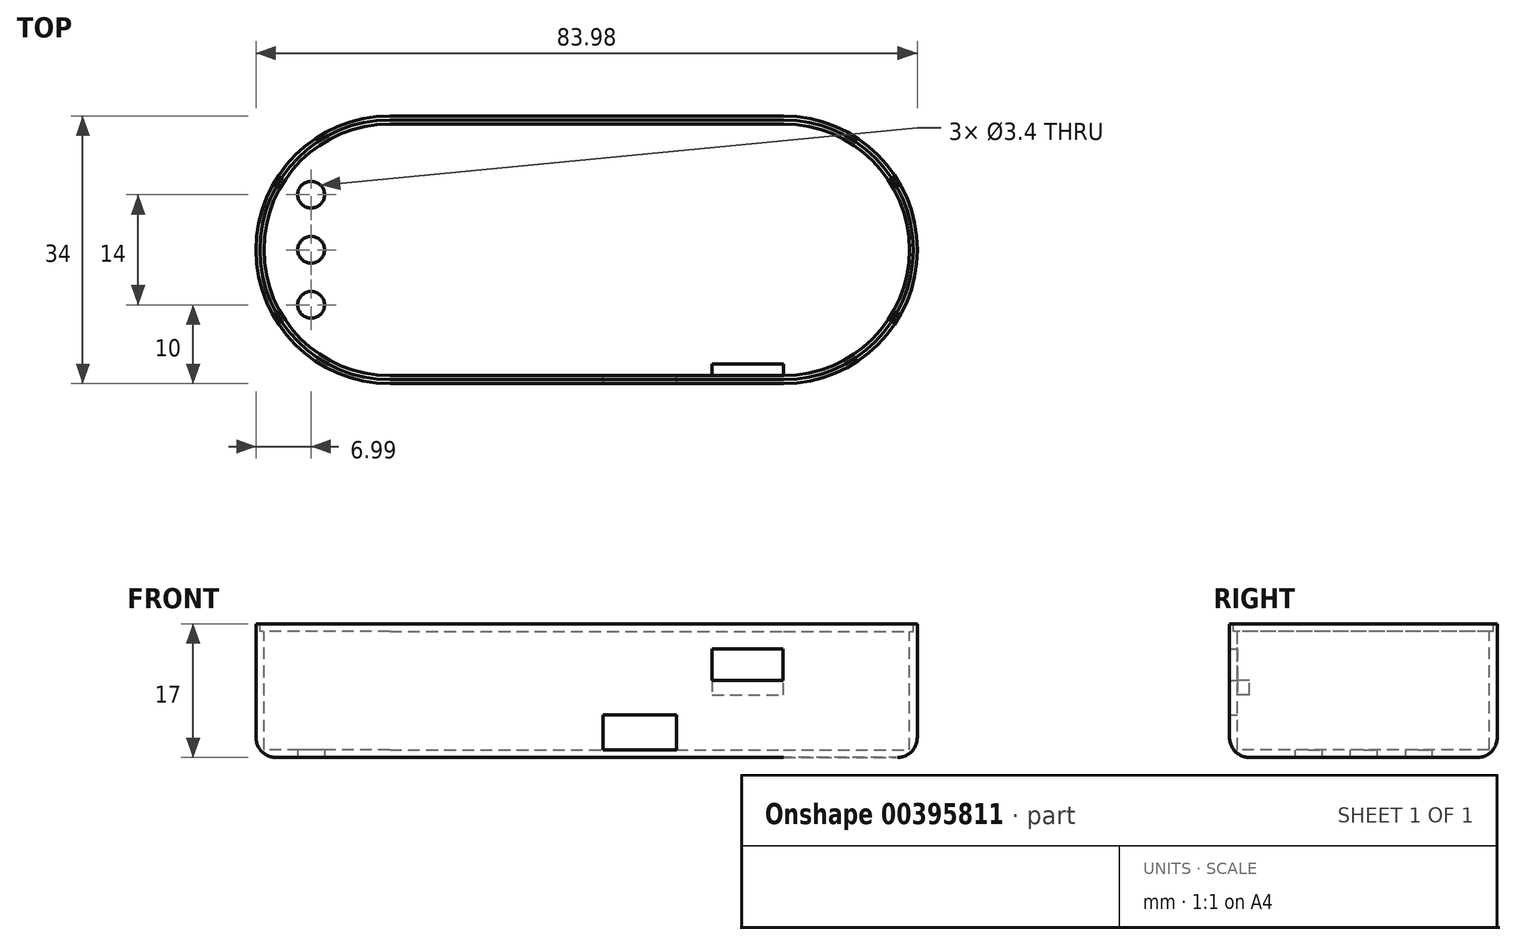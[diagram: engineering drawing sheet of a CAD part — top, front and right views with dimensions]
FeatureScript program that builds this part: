
annotation { "Feature Type Name" : "Feature", "Feature Type Description" : "" }
export const myFeature = defineFeature(function(context is Context, id is Id, definition is map)
    precondition{}
    {
        {
            var Q0;
            Q0=qCreatedBy(makeId("Top.planeOp"),FACE);
            var sketch = newSketch(context, id + "F0", { "sketchPlane" : qUnion([Q0])});
            skLineSegment(sketch, "E0.bottom", {"start": v(-25, 17) * mm, "end": v(25, 17) * mm});
            skLineSegment(sketch, "E0.top", {"start": v(-25, -17) * mm, "end": v(25, -17) * mm});
            skPoint(sketch, "E0.middle", {"position": v(0, 0) * mm});
            skPoint(sketch, "E1", {"position": v(25, 0) * mm});
            skPoint(sketch, "E2", {"position": v(-25, 0) * mm});
            skArc(sketch, "E3", {"start": v(-25, 17) * mm, "mid": v(-42, 0) * mm, "end": v(-25, -17) * mm});
            skArc(sketch, "E4", {"start": v(25, 17) * mm, "mid": v(42, 0) * mm, "end": v(25, -17) * mm});
            skPoint(sketch, "E5", {"position": v(-42, 0) * mm});
            skPoint(sketch, "E6", {"position": v(42, 0) * mm});
            skSolve(sketch);
        }
        {
            var Q0;
            Q0 = qSketchRegion(id + "F0", true);
            extrude(context, id + "F1", {"entities" : qUnion([Q0]), "offsetDistance" : 25.4 * mm, "depth" : 17 * mm});
        }
        {
            var Q0;
            Q0=makeQuery(id+"F1.opExtrude","CAP_FACE",FACE,{"disambiguationData":[OSD([sQuery(id+"F0.wireOp",EDGE,"E0.bottom"),sQuery(id+"F0.wireOp",EDGE,"E0.top"),sQuery(id+"F0.wireOp",EDGE,"E3"),sQuery(id+"F0.wireOp",EDGE,"E4")])],"isStart":false});
            var sketch = newSketch(context, id + "F2", { "sketchPlane" : qUnion([Q0])});
            skPoint(sketch, "E7", {"position": v(-25, 16.5) * mm});
            skPoint(sketch, "E8", {"position": v(25, 16.5) * mm});
            skPoint(sketch, "E9", {"position": v(-25, -16.5) * mm});
            skPoint(sketch, "E10", {"position": v(25, -16.5) * mm});
            skLineSegment(sketch, "E11.bottom", {"start": v(-25, 16.5) * mm, "end": v(25, 16.5) * mm});
            skLineSegment(sketch, "E11.top", {"start": v(-25, -16.5) * mm, "end": v(25, -16.5) * mm});
            skArc(sketch, "E12", {"start": v(-25, 16.5) * mm, "mid": v(-41.5, 0) * mm, "end": v(-25, -16.5) * mm});
            skArc(sketch, "E13", {"start": v(25, 16.5) * mm, "mid": v(41.5, 0) * mm, "end": v(25, -16.5) * mm});
            skSolve(sketch);
        }
        {
            var Q0;
            Q0 = qSketchRegion(id + "F2", true);
            extrude(context, id + "F3", {"entities" : qUnion([Q0]), "operationType" : NewBodyOperationType.REMOVE, "oppositeDirection" : true, "depth" : 1 * mm});
        }
        {
            var Q0;
            Q0=makeQuery(id+"F3.boolean.opBoolean","COPY",FACE,{"derivedFrom":makeQuery(id+"F3.opExtrude","CAP_FACE",FACE,{"disambiguationData":[OSD([sQuery(id+"F2.wireOp",EDGE,"E11.bottom"),sQuery(id+"F2.wireOp",EDGE,"E11.top"),sQuery(id+"F2.wireOp",EDGE,"E12"),sQuery(id+"F2.wireOp",EDGE,"E13")])],"isStart":false})});
            var sketch = newSketch(context, id + "F4", { "sketchPlane" : qUnion([Q0])});
            skPoint(sketch, "E14", {"position": v(-25, 16) * mm});
            skPoint(sketch, "E15", {"position": v(-25, -16) * mm});
            skPoint(sketch, "E16", {"position": v(25, 16) * mm});
            skPoint(sketch, "E17", {"position": v(25, -16) * mm});
            skArc(sketch, "E18", {"start": v(-25, 16) * mm, "mid": v(-41, 0) * mm, "end": v(-25, -16) * mm});
            skArc(sketch, "E19", {"start": v(25, 16) * mm, "mid": v(41, 0) * mm, "end": v(25, -16) * mm});
            skLineSegment(sketch, "E20", {"start": v(-25, 16) * mm, "end": v(25, 16) * mm});
            skLineSegment(sketch, "E21", {"start": v(-25, -16) * mm, "end": v(25, -16) * mm});
            skSolve(sketch);
        }
        {
            var Q0;
            Q0 = qSketchRegion(id + "F4", true);
            extrude(context, id + "F5", {"entities" : qUnion([Q0]), "operationType" : NewBodyOperationType.REMOVE, "oppositeDirection" : true, "depth" : 15 * mm});
        }
        {
            var Q0;
            Q0=makeQuery(id+"F1.opExtrude","CAP_FACE",FACE,{"disambiguationData":[OSD([sQuery(id+"F0.wireOp",EDGE,"E0.bottom"),sQuery(id+"F0.wireOp",EDGE,"E0.top"),sQuery(id+"F0.wireOp",EDGE,"E3"),sQuery(id+"F0.wireOp",EDGE,"E4")])],"isStart":true});
            var sketch = newSketch(context, id + "F6", { "sketchPlane" : qUnion([Q0])});
            skPoint(sketch, "E22", {"position": v(-35, 7) * mm});
            skPoint(sketch, "E23", {"position": v(-35, 0) * mm});
            skPoint(sketch, "E24", {"position": v(-35, -7) * mm});
            skCircle(sketch, "E25", {"center": v(-35, -7) * mm, "radius": 1.7 * mm});
            skPoint(sketch, "E26", {"position": v(0, 7) * mm});
            skPoint(sketch, "E27", {"position": v(0, -7) * mm});
            skCircle(sketch, "E28", {"center": v(-35, 0) * mm, "radius": 1.7 * mm});
            skCircle(sketch, "E29", {"center": v(-35, 7) * mm, "radius": 1.7 * mm});
            skLineSegment(sketch, "E30", {"start": v(-35, -7) * mm, "end": v(0, -7) * mm});
            skLineSegment(sketch, "E31", {"start": v(0, 0) * mm, "end": v(-35, 0) * mm});
            skLineSegment(sketch, "E32", {"start": v(-30.27, -15.26) * mm, "end": v(-30.27, 14.86) * mm});
            skSolve(sketch);
        }
        {
            var Q0;
            Q0=makeQuery(id+"F5.boolean.opBoolean","COPY",FACE,{"derivedFrom":makeQuery(id+"F5.opExtrude","SWEPT_FACE",FACE,{"disambiguationData":[OSD([sQuery(id+"F4.wireOp",EDGE,"E21")])]})});
            var sketch = newSketch(context, id + "F7", { "sketchPlane" : qUnion([Q0])});
            skPoint(sketch, "E33", {"position": v(-11.39, 1) * mm});
            skLineSegment(sketch, "E34.left", {"start": v(-11.39, 1) * mm, "end": v(-11.39, 5.4) * mm});
            skLineSegment(sketch, "E35.bottom", {"start": v(-15.94, 13.82) * mm, "end": v(-24.94, 13.82) * mm});
            skLineSegment(sketch, "E35.top", {"start": v(-15.94, 9.82) * mm, "end": v(-24.94, 9.82) * mm});
            skLineSegment(sketch, "E35.left", {"start": v(-15.94, 13.82) * mm, "end": v(-15.94, 9.82) * mm});
            skLineSegment(sketch, "E35.right", {"start": v(-24.94, 13.82) * mm, "end": v(-24.94, 9.82) * mm});
            skPoint(sketch, "E36.orphan", {"position": v(-20.99, 10.26) * mm});
            skPoint(sketch, "E37.orphan", {"position": v(-20.99, 16.75) * mm});
            skPoint(sketch, "E38", {"position": v(-2.09, 1) * mm});
            skLineSegment(sketch, "E39.bottom", {"start": v(-2.09, 1) * mm, "end": v(-11.39, 1) * mm});
            skLineSegment(sketch, "E39.top", {"start": v(-2.09, 5.4) * mm, "end": v(-11.39, 5.4) * mm});
            skLineSegment(sketch, "E39.left", {"start": v(-2.09, 1) * mm, "end": v(-2.09, 5.4) * mm});
            skLineSegment(sketch, "E40.bottom", {"start": v(-15.94, 9.82) * mm, "end": v(-25, 9.82) * mm});
            skLineSegment(sketch, "E40.top", {"start": v(-15.94, 7.17) * mm, "end": v(-25, 7.17) * mm});
            skLineSegment(sketch, "E40.left", {"start": v(-15.94, 9.82) * mm, "end": v(-15.94, 7.17) * mm});
            skLineSegment(sketch, "E40.right", {"start": v(-25, 9.82) * mm, "end": v(-25, 7.17) * mm});
            skSolve(sketch);
        }
        {
            var Q0;
            Q0=makeQuery(id+"F7.imprint","IMPRINT",FACE,{"disambiguationData":[TD([[makeQuery(id+"F7.imprint","IMPRINT",EDGE,{"derivedFrom":sQuery(id+"F7.wireOp",EDGE,"E34.bottom")}),-1.0]])]});
            var Q1;
            Q1=makeQuery(id+"F7.imprint","IMPRINT",FACE,{"disambiguationData":[TD([[makeQuery(id+"F7.imprint","IMPRINT",EDGE,{"derivedFrom":sQuery(id+"F7.wireOp",EDGE,"E35.bottom")}),1.0]])]});
            var Q2;
            Q2=makeQuery(id+"F7.imprint","IMPRINT",FACE,{"disambiguationData":[TD([[makeQuery(id+"F7.imprint","IMPRINT",EDGE,{"derivedFrom":sQuery(id+"F7.wireOp",EDGE,"E34.left")}),-1.0]])]});
            extrude(context, id + "F8", {"entities" : qUnion([Q0, Q1, Q2]), "operationType" : NewBodyOperationType.REMOVE, "endBound" : BoundingType.THROUGH_ALL, "oppositeDirection" : true, "depth" : 25.4 * mm});
        }
        {
            var Q0;
            Q0=makeQuery(id+"F5.boolean.opBoolean","COPY",FACE,{"derivedFrom":makeQuery(id+"F5.opExtrude","SWEPT_FACE",FACE,{"disambiguationData":[OSD([sQuery(id+"F4.wireOp",EDGE,"E21")])]})});
            var sketch = newSketch(context, id + "F9", { "sketchPlane" : qUnion([Q0])});
            skLineSegment(sketch, "E41.bottom", {"start": v(-15.94, 9.82) * mm, "end": v(-25, 9.82) * mm});
            skLineSegment(sketch, "E41.top", {"start": v(-15.94, 7.96) * mm, "end": v(-25, 7.96) * mm});
            skLineSegment(sketch, "E41.left", {"start": v(-15.94, 9.82) * mm, "end": v(-15.94, 7.96) * mm});
            skLineSegment(sketch, "E41.right", {"start": v(-25, 9.82) * mm, "end": v(-25, 7.96) * mm});
            skSolve(sketch);
        }
        {
            var Q0;
            Q0 = qSketchRegion(id + "F9", true);
            extrude(context, id + "F10", {"entities" : qUnion([Q0]), "operationType" : NewBodyOperationType.ADD, "depth" : 1.5 * mm, "offsetDistance" : 25.4 * mm});
        }
        {
            var Q0;
            Q0 = qSketchRegion(id + "F6", true);
            extrude(context, id + "F11", {"entities" : qUnion([Q0]), "operationType" : NewBodyOperationType.REMOVE, "endBound" : BoundingType.THROUGH_ALL, "oppositeDirection" : true, "depth" : 25.4 * mm});
        }
        {
            var Q0;
            Q0=makeQuery(id+"F1.opExtrude","CAP_EDGE",EDGE,{"disambiguationData":[OSD([sQuery(id+"F0.wireOp",EDGE,"E3")])],"isStart":true});
            fillet(context, id + "F12", {"entities" : qUnion([Q0]), "tangentPropagation" : true, "radius" : 2.54 * mm, "defaultsChanged" : true, "vertexSettings" : [], "allowEdgeOverflow" : false});
        }
    });
